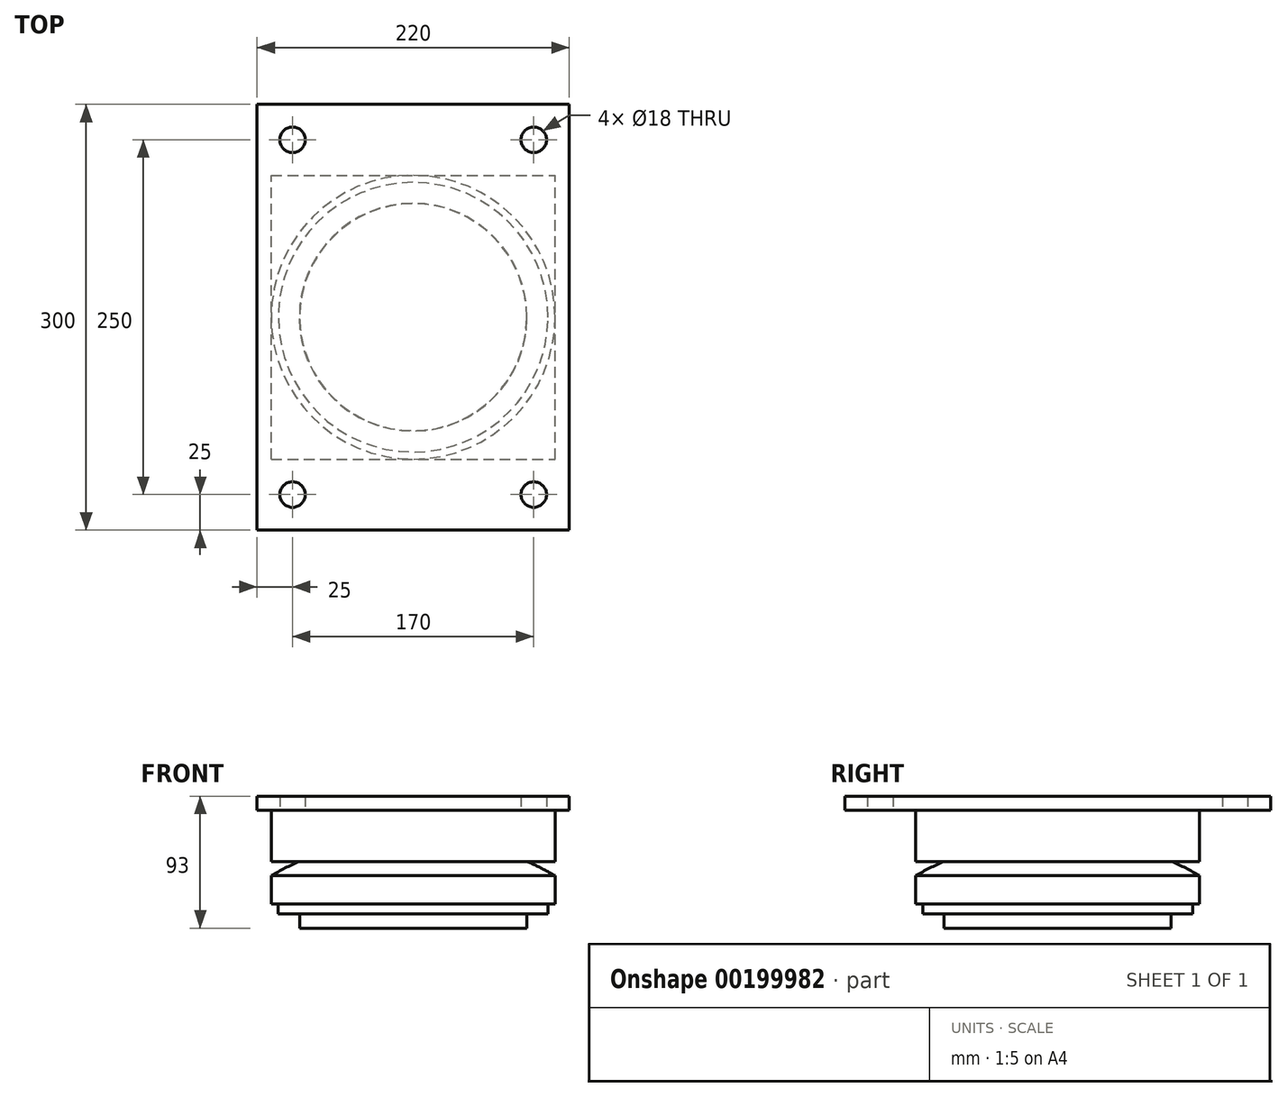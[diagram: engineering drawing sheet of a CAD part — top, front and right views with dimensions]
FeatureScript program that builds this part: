
annotation { "Feature Type Name" : "Feature", "Feature Type Description" : "" }
export const myFeature = defineFeature(function(context is Context, id is Id, definition is map)
    precondition{}
    {
        {
            var Q0;
            Q0=qCreatedBy(makeId("Top.planeOp"),FACE);
            var sketch = newSketch(context, id + "F0", { "sketchPlane" : qUnion([Q0])});
            skLineSegment(sketch, "E0.bottom", {"start": v(-110, 150) * mm, "end": v(110, 150) * mm});
            skLineSegment(sketch, "E0.top", {"start": v(-110, -150) * mm, "end": v(110, -150) * mm});
            skLineSegment(sketch, "E0.left", {"start": v(-110, 150) * mm, "end": v(-110, -150) * mm});
            skLineSegment(sketch, "E0.right", {"start": v(110, 150) * mm, "end": v(110, -150) * mm});
            skCircle(sketch, "E1", {"center": v(-85, 125) * mm, "radius": 9 * mm});
            skCircle(sketch, "E2", {"center": v(85, 125) * mm, "radius": 9 * mm});
            skCircle(sketch, "E3", {"center": v(-85, -125) * mm, "radius": 9 * mm});
            skCircle(sketch, "E4", {"center": v(85, -125) * mm, "radius": 9 * mm});
            skLineSegment(sketch, "E5", {"start": v(0, 0) * mm, "end": v(-110, 0) * mm, "construction": true});
            skSolve(sketch);
        }
        {
            var Q0;
            Q0 = qSketchRegion(id + "F0", true);
            extrude(context, id + "F1", {"entities" : qUnion([Q0]), "depth" : 10 * mm});
        }
        {
            var Q0;
            Q0=makeQuery(id+"F1.opExtrude","CAP_FACE",FACE,{"disambiguationData":[OSD([sQuery(id+"F0.wireOp",EDGE,"E0.bottom"),sQuery(id+"F0.wireOp",EDGE,"E0.top"),sQuery(id+"F0.wireOp",EDGE,"E0.left"),sQuery(id+"F0.wireOp",EDGE,"E0.right"),sQuery(id+"F0.wireOp",EDGE,"E1"),sQuery(id+"F0.wireOp",EDGE,"E2"),sQuery(id+"F0.wireOp",EDGE,"E3"),sQuery(id+"F0.wireOp",EDGE,"E4")])],"isStart":true});
            var sketch = newSketch(context, id + "F2", { "sketchPlane" : qUnion([Q0])});
            skLineSegment(sketch, "E6.bottom", {"start": v(-100, 100) * mm, "end": v(100, 100) * mm});
            skLineSegment(sketch, "E6.top", {"start": v(-100, -100) * mm, "end": v(100, -100) * mm});
            skLineSegment(sketch, "E6.left", {"start": v(-100, 100) * mm, "end": v(-100, -100) * mm});
            skLineSegment(sketch, "E6.right", {"start": v(100, 100) * mm, "end": v(100, -100) * mm});
            skLineSegment(sketch, "E7", {"start": v(0, 0) * mm, "end": v(-100, 0) * mm, "construction": true});
            skSolve(sketch);
        }
        {
            var Q0;
            Q0 = qSketchRegion(id + "F2", true);
            extrude(context, id + "F3", {"entities" : qUnion([Q0]), "operationType" : NewBodyOperationType.ADD, "depth" : 36 * mm});
        }
        {
            var Q0;
            Q0=qCreatedBy(makeId("Right.planeOp"),FACE);
            var sketch = newSketch(context, id + "F4", { "sketchPlane" : qUnion([Q0])});
            skLineSegment(sketch, "E8", {"start": v(0, 0) * mm, "end": v(0, -83) * mm, "construction": true});
            skLineSegment(sketch, "E9", {"start": v(100, -46) * mm, "end": v(100, -66) * mm});
            skLineSegment(sketch, "E10", {"start": v(100, -66) * mm, "end": v(95, -66) * mm});
            skLineSegment(sketch, "E11", {"start": v(95, -66) * mm, "end": v(95, -73) * mm});
            skLineSegment(sketch, "E12", {"start": v(95, -73) * mm, "end": v(80, -73) * mm});
            skLineSegment(sketch, "E13", {"start": v(80, -73) * mm, "end": v(80, -83) * mm});
            skLineSegment(sketch, "E14", {"start": v(80, -83) * mm, "end": v(0, -83) * mm});
            skArc(sketch, "E15", {"start": v(100, -46) * mm, "mid": v(90.25, -40.73) * mm, "end": v(80.22, -36) * mm});
            skLineSegment(sketch, "E16", {"start": v(80.22, -36) * mm, "end": v(0, -36) * mm});
            skLineSegment(sketch, "E17", {"start": v(0, -83) * mm, "end": v(0, -36) * mm});
            skSolve(sketch);
        }
        {
            var Q0;
            Q0 = qSketchRegion(id + "F4", true);
            var Q1;
            Q1=sQuery(id+"F4.wireOp",EDGE,"E8");
            revolve(context, id + "F5", {"operationType" : NewBodyOperationType.ADD, "entities" : qUnion([Q0]), "axis" : qUnion([Q1]), "revolveType" : RevolveType.FULL});
        }
    });
